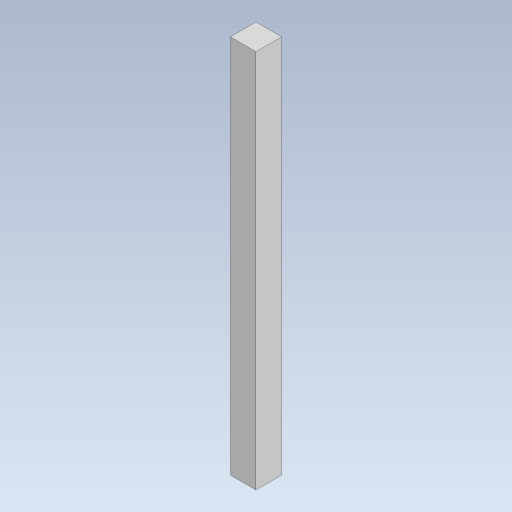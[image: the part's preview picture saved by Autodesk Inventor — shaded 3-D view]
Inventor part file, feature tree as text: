
AUTODESK INVENTOR PART (.ipt)
format: ipt  version: 2023 (Build 270158000, 158)  size: 78,848 bytes
history: native  units: in
note: dims shown in document units (in); Inventor stores cm internally (conversion verified against a paired STEP export)
features: extrude x1, sketch x1
ambient origin geometry x8: Origin, YZ Plane, XZ Plane, XY Plane, X Axis, Y Axis, Z Axis, Center Point
bodies: Solid1 (feature_tree)
feature tree (2):
  extrude  "Extrusion1"  Depth=0.3937in
  sketch  "Sketch1"  dims[d0=0.3937in d1=0.3937in d2=5.8268in d3=0.0in]
